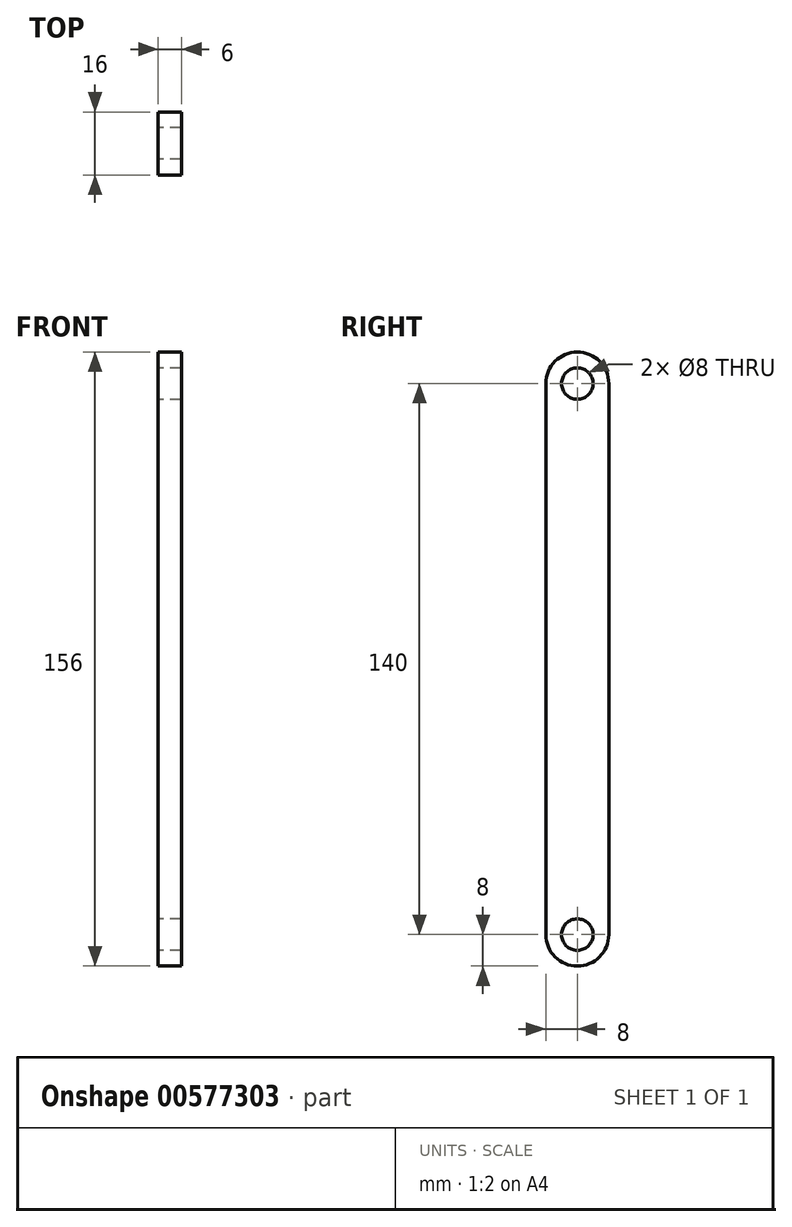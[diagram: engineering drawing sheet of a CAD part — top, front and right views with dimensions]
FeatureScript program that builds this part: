
annotation { "Feature Type Name" : "Feature", "Feature Type Description" : "" }
export const myFeature = defineFeature(function(context is Context, id is Id, definition is map)
    precondition{}
    {
        {
            var Q0;
            Q0=qCreatedBy(makeId("Right.planeOp"),FACE);
            var sketch = newSketch(context, id + "F0", { "sketchPlane" : qUnion([Q0])});
            skArc(sketch, "E0", {"start": v(8, 0) * mm, "mid": v(0, 8) * mm, "end": v(-8, 0) * mm});
            skArc(sketch, "E1", {"start": v(-8, -140) * mm, "mid": v(0, -148) * mm, "end": v(8, -140) * mm});
            skLineSegment(sketch, "E2", {"start": v(-8, -140) * mm, "end": v(-8, 0) * mm});
            skLineSegment(sketch, "E3", {"start": v(8, -140) * mm, "end": v(8, 0) * mm});
            skCircle(sketch, "E4", {"center": v(0, -140) * mm, "radius": 4 * mm});
            skCircle(sketch, "E5", {"center": v(0, 0) * mm, "radius": 4 * mm});
            skSolve(sketch);
        }
        {
            var Q0;
            Q0 = qSketchRegion(id + "F0", true);
            extrude(context, id + "F1", {"entities" : qUnion([Q0]), "depth" : 6 * mm, "offsetDistance" : 25 * mm});
        }
    });
